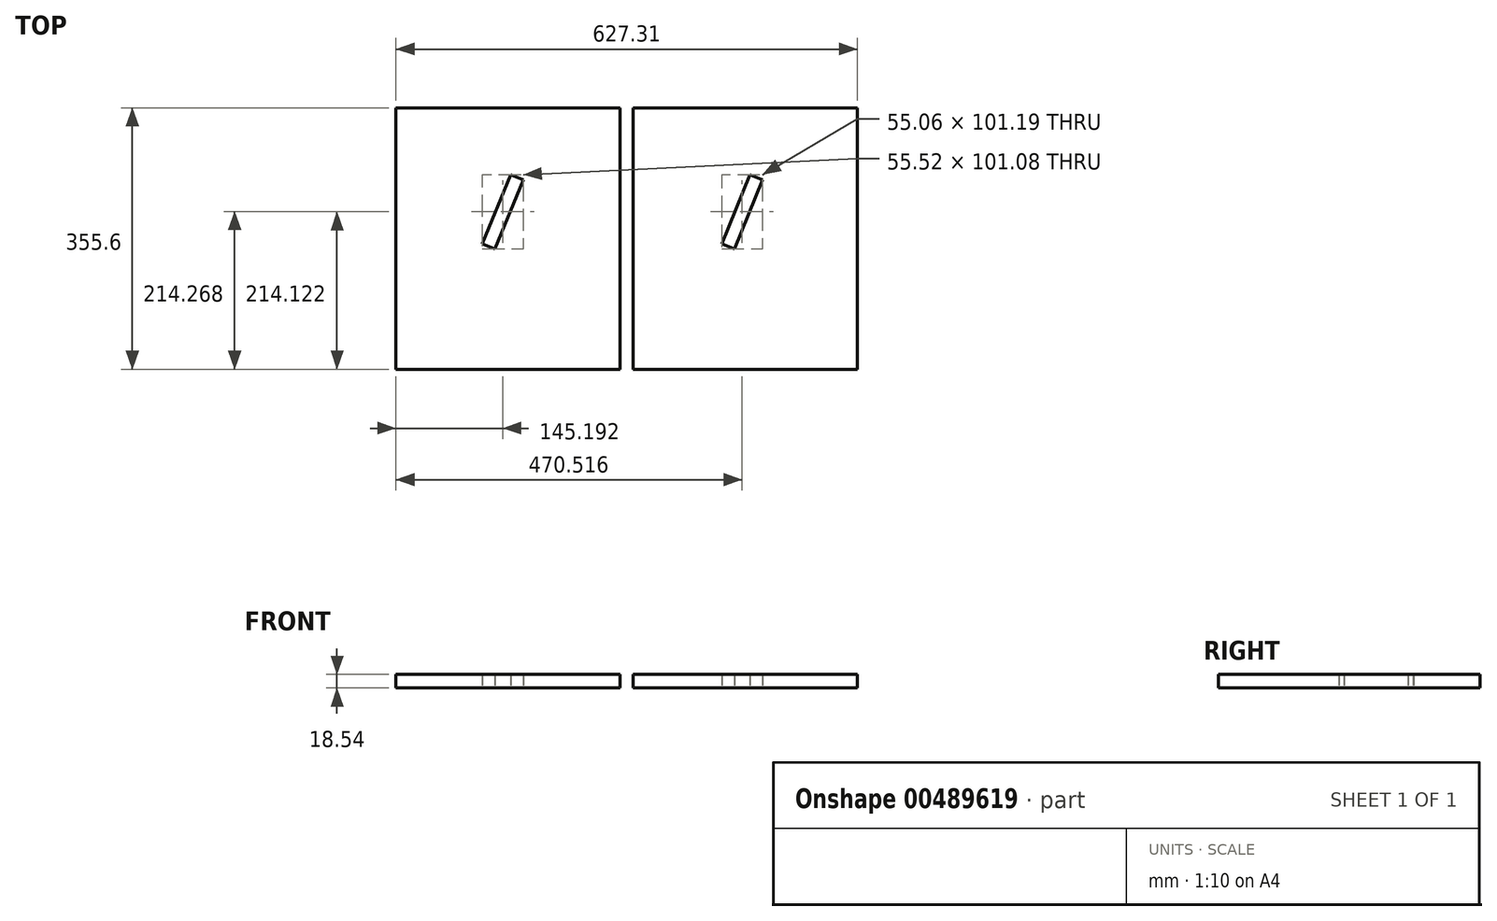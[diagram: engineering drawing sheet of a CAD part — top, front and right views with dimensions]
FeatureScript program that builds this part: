
annotation { "Feature Type Name" : "Feature", "Feature Type Description" : "" }
export const myFeature = defineFeature(function(context is Context, id is Id, definition is map)
    precondition{}
    {
        {
            var Q0;
            Q0=qCreatedBy(makeId("Top.planeOp"),FACE);
            var sketch = newSketch(context, id + "F0", { "sketchPlane" : qUnion([Q0])});
            skLineSegment(sketch, "E0.bottom", {"start": v(-322.5, 0) * mm, "end": v(-17.7, 0) * mm});
            skLineSegment(sketch, "E0.top", {"start": v(-322.5, 355.6) * mm, "end": v(-17.7, 355.6) * mm});
            skLineSegment(sketch, "E0.left", {"start": v(-322.5, 0) * mm, "end": v(-322.5, 355.6) * mm});
            skLineSegment(sketch, "E0.right", {"start": v(-17.7, 0) * mm, "end": v(-17.7, 355.6) * mm});
            skLineSegment(sketch, "E1", {"start": v(-322.5, 0) * mm, "end": v(-297.1, 0) * mm});
            skLineSegment(sketch, "E2", {"start": v(-17.7, 0) * mm, "end": v(-30.4, 0) * mm});
            skLineSegment(sketch, "E3.bottom", {"start": v(-297.1, 0) * mm, "end": v(-208.2, 0) * mm});
            skLineSegment(sketch, "E3.top", {"start": v(-297.1, -18.54) * mm, "end": v(-208.2, -18.54) * mm});
            skLineSegment(sketch, "E3.left", {"start": v(-297.1, 0) * mm, "end": v(-297.1, -18.54) * mm});
            skLineSegment(sketch, "E3.right", {"start": v(-208.2, 0) * mm, "end": v(-208.2, -18.54) * mm});
            skLineSegment(sketch, "E4", {"start": v(-208.2, 0) * mm, "end": v(-119.3, 0) * mm});
            skLineSegment(sketch, "E5.bottom", {"start": v(-119.3, 0) * mm, "end": v(-30.4, 0) * mm});
            skLineSegment(sketch, "E5.top", {"start": v(-119.3, -18.54) * mm, "end": v(-30.4, -18.54) * mm});
            skLineSegment(sketch, "E5.left", {"start": v(-119.3, 0) * mm, "end": v(-119.3, -18.54) * mm});
            skLineSegment(sketch, "E5.right", {"start": v(-30.4, 0) * mm, "end": v(-30.4, -18.54) * mm});
            skLineSegment(sketch, "E6", {"start": v(-17.7, 355.6) * mm, "end": v(-17.7, 177.8) * mm});
            skLineSegment(sketch, "E7", {"start": v(-17.7, 177.8) * mm, "end": v(-17.7, 203.2) * mm});
            skLineSegment(sketch, "E8.left", {"start": v(-17.7, 203.2) * mm, "end": v(-17.7, 152.4) * mm});
            skLineSegment(sketch, "E9.bottom", {"start": v(-119.3, 228.6) * mm, "end": v(-119.3, 228.6) * mm});
            skLineSegment(sketch, "E9.top", {"start": v(-119.3, 355.6) * mm, "end": v(-119.3, 355.6) * mm});
            skLineSegment(sketch, "E10", {"start": v(-205.08, 170.73) * mm, "end": v(-166.73, 264.8) * mm});
            skLineSegment(sketch, "E11", {"start": v(-166.73, 264.8) * mm, "end": v(-149.56, 257.81) * mm});
            skLineSegment(sketch, "E12", {"start": v(-149.56, 257.81) * mm, "end": v(-187.9, 163.73) * mm});
            skLineSegment(sketch, "E13", {"start": v(-205.08, 170.73) * mm, "end": v(-187.9, 163.73) * mm});
            skSolve(sketch);
        }
        {
            var Q0;
            Q0=makeQuery(id+"F0.imprint","IMPRINT",FACE,{"disambiguationData":[TD([[makeQuery(id+"F0.imprint","IMPRINT",EDGE,{"derivedFrom":sQuery(id+"F0.wireOp",EDGE,"E0.top")}),-1.0]])]});
            var Q1;
            Q1=makeQuery(id+"F0.imprint","IMPRINT",FACE,{"disambiguationData":[TD([[makeQuery(id+"F0.imprint","IMPRINT",EDGE,{"derivedFrom":sQuery(id+"F0.wireOp",EDGE,"E3.bottom")}),-1.0]])]});
            var Q2;
            Q2=makeQuery(id+"F0.imprint","IMPRINT",FACE,{"disambiguationData":[TD([[makeQuery(id+"F0.imprint","IMPRINT",EDGE,{"derivedFrom":sQuery(id+"F0.wireOp",EDGE,"E5.bottom")}),-1.0]])]});
            extrude(context, id + "F1", {"entities" : qUnion([Q0, Q1, Q2]), "depth" : 18.54 * mm, "offsetDistance" : 25.4 * mm});
        }
        {
            var Q0;
            Q0=qCreatedBy(makeId("Top.planeOp"),FACE);
            var sketch = newSketch(context, id + "F2", { "sketchPlane" : qUnion([Q0])});
            skLineSegment(sketch, "E14.bottom", {"start": v(0, 0) * mm, "end": v(304.8, 0) * mm});
            skLineSegment(sketch, "E14.top", {"start": v(0, 355.6) * mm, "end": v(304.8, 355.6) * mm});
            skLineSegment(sketch, "E14.left", {"start": v(0, 0) * mm, "end": v(0, 355.6) * mm});
            skLineSegment(sketch, "E14.right", {"start": v(304.8, 0) * mm, "end": v(304.8, 355.6) * mm});
            skLineSegment(sketch, "E15", {"start": v(0, 0) * mm, "end": v(25.4, 0) * mm});
            skLineSegment(sketch, "E16", {"start": v(304.8, 0) * mm, "end": v(292.1, 0) * mm});
            skLineSegment(sketch, "E17.bottom", {"start": v(25.4, 0) * mm, "end": v(114.3, 0) * mm});
            skLineSegment(sketch, "E17.top", {"start": v(25.4, -18.54) * mm, "end": v(114.3, -18.54) * mm});
            skLineSegment(sketch, "E17.left", {"start": v(25.4, 0) * mm, "end": v(25.4, -18.54) * mm});
            skLineSegment(sketch, "E17.right", {"start": v(114.3, 0) * mm, "end": v(114.3, -18.54) * mm});
            skLineSegment(sketch, "E18.bottom", {"start": v(292.1, 0) * mm, "end": v(203.2, 0) * mm});
            skLineSegment(sketch, "E18.top", {"start": v(292.1, -18.54) * mm, "end": v(203.2, -18.54) * mm});
            skLineSegment(sketch, "E18.left", {"start": v(292.1, 0) * mm, "end": v(292.1, -18.54) * mm});
            skLineSegment(sketch, "E18.right", {"start": v(203.2, 0) * mm, "end": v(203.2, -18.54) * mm});
            skLineSegment(sketch, "E19", {"start": v(114.3, -18.54) * mm, "end": v(203.2, -18.54) * mm});
            skLineSegment(sketch, "E20", {"start": v(304.8, 355.6) * mm, "end": v(304.8, 177.8) * mm});
            skLineSegment(sketch, "E21.bottom", {"start": v(304.8, 355.6) * mm, "end": v(304.8, 355.6) * mm});
            skLineSegment(sketch, "E21.top", {"start": v(304.8, 177.8) * mm, "end": v(304.8, 177.8) * mm});
            skLineSegment(sketch, "E22.right", {"start": v(279.4, 177.8) * mm, "end": v(279.4, 177.8) * mm});
            skLineSegment(sketch, "E23", {"start": v(120.47, 170.43) * mm, "end": v(158.33, 264.72) * mm});
            skLineSegment(sketch, "E24", {"start": v(158.33, 264.72) * mm, "end": v(175.54, 257.81) * mm});
            skLineSegment(sketch, "E25", {"start": v(120.47, 170.43) * mm, "end": v(137.68, 163.53) * mm});
            skLineSegment(sketch, "E26", {"start": v(137.68, 163.53) * mm, "end": v(175.54, 257.81) * mm});
            skSolve(sketch);
        }
        {
            var Q0;
            Q0=makeQuery(id+"F2.imprint","IMPRINT",FACE,{"disambiguationData":[TD([[makeQuery(id+"F2.imprint","IMPRINT",EDGE,{"derivedFrom":sQuery(id+"F2.wireOp",EDGE,"E14.bottom")}),1.0]])]});
            var Q1;
            Q1=makeQuery(id+"F2.imprint","IMPRINT",FACE,{"disambiguationData":[TD([[makeQuery(id+"F2.imprint","IMPRINT",EDGE,{"derivedFrom":sQuery(id+"F2.wireOp",EDGE,"E18.bottom")}),1.0]])]});
            var Q2;
            Q2=makeQuery(id+"F2.imprint","IMPRINT",FACE,{"disambiguationData":[TD([[makeQuery(id+"F2.imprint","IMPRINT",EDGE,{"derivedFrom":sQuery(id+"F2.wireOp",EDGE,"E17.bottom")}),-1.0]])]});
            extrude(context, id + "F3", {"entities" : qUnion([Q0, Q1, Q2]), "depth" : 18.54 * mm, "offsetDistance" : 25.4 * mm});
        }
    });
